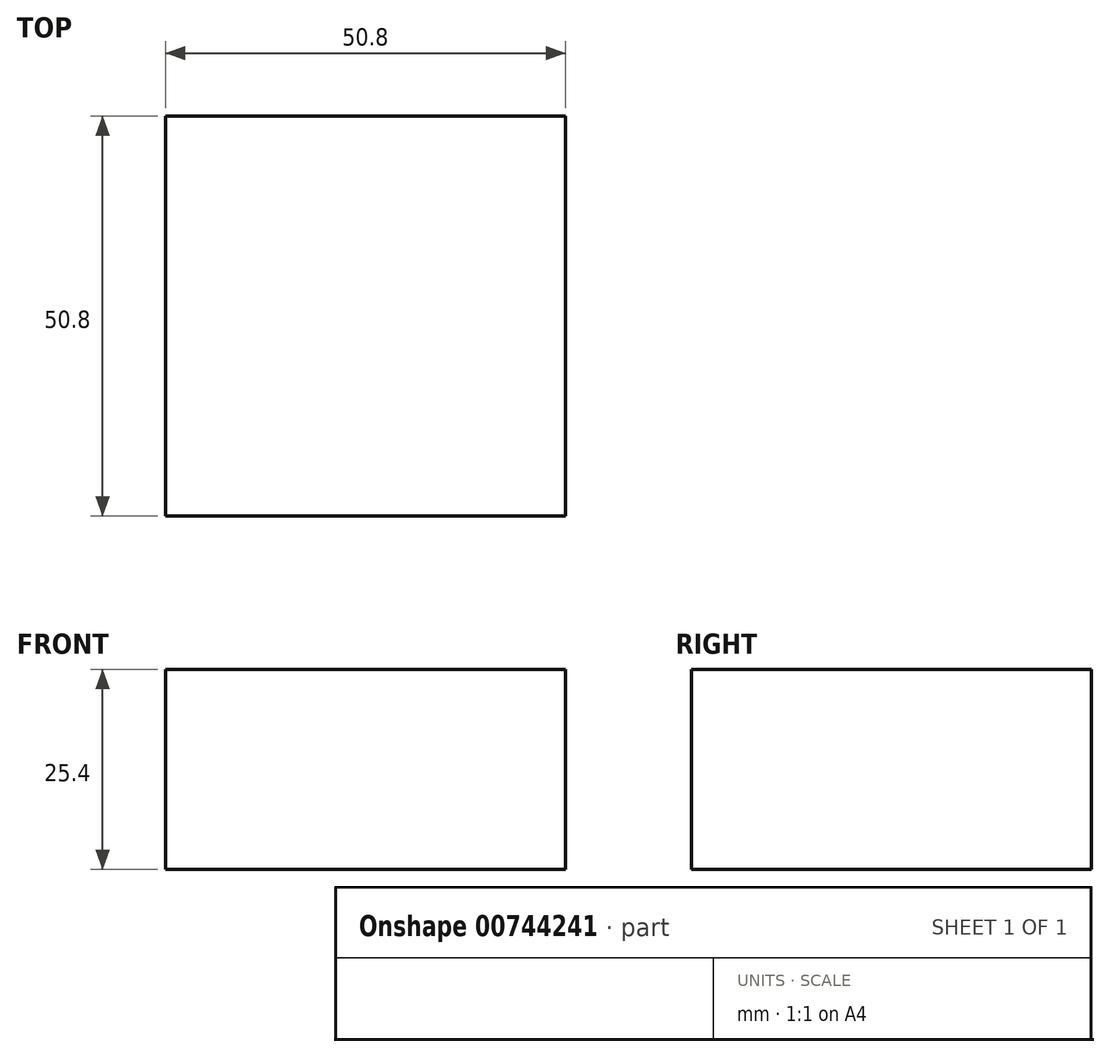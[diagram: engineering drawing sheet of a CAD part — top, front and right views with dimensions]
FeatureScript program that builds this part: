
annotation { "Feature Type Name" : "Feature", "Feature Type Description" : "" }
export const myFeature = defineFeature(function(context is Context, id is Id, definition is map)
    precondition{}
    {
        {
            var Q0;
            Q0=qCreatedBy(makeId("Top.planeOp"),FACE);
            var sketch = newSketch(context, id + "F0", { "sketchPlane" : qUnion([Q0])});
            skLineSegment(sketch, "E0.bottom", {"start": v(0, 0) * mm, "end": v(50.8, 0) * mm});
            skLineSegment(sketch, "E0.top", {"start": v(0, 50.8) * mm, "end": v(50.8, 50.8) * mm});
            skLineSegment(sketch, "E0.left", {"start": v(0, 0) * mm, "end": v(0, 50.8) * mm});
            skLineSegment(sketch, "E0.right", {"start": v(50.8, 0) * mm, "end": v(50.8, 50.8) * mm});
            skSolve(sketch);
        }
        {
            var Q0;
            Q0 = qSketchRegion(id + "F0", true);
            extrude(context, id + "F1", {"entities" : qUnion([Q0]), "depth" : 25.4 * mm, "offsetDistance" : 25.4 * mm});
        }
    });
